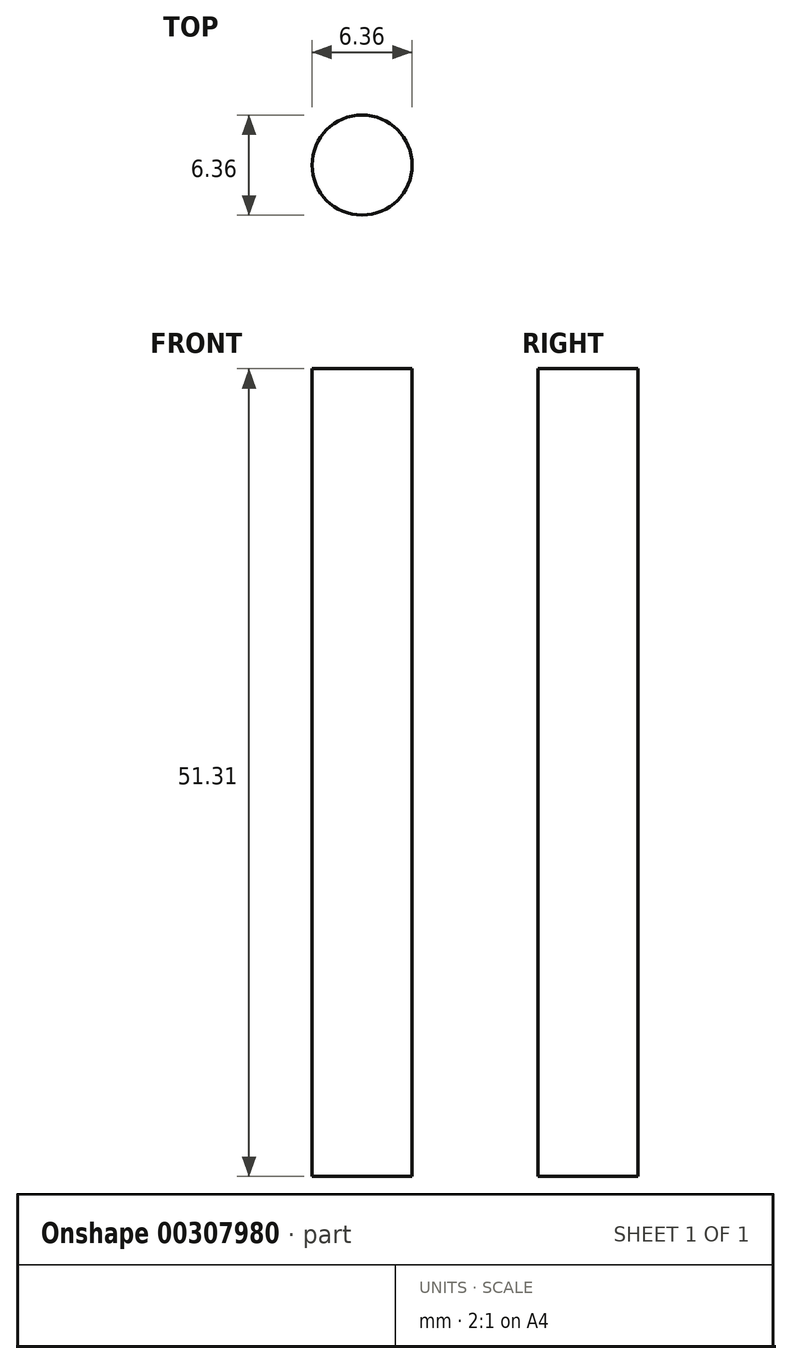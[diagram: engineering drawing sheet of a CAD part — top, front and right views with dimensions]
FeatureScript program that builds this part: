
annotation { "Feature Type Name" : "Feature", "Feature Type Description" : "" }
export const myFeature = defineFeature(function(context is Context, id is Id, definition is map)
    precondition{}
    {
        {
            var Q0;
            Q0=qCreatedBy(makeId("Top.planeOp"),FACE);
            var sketch = newSketch(context, id + "F0", { "sketchPlane" : qUnion([Q0])});
            skCircle(sketch, "E0", {"center": v(0, 0) * mm, "radius": 3.17 * mm});
            skSolve(sketch);
        }
        {
            var Q0;
            Q0 = qSketchRegion(id + "F0", true);
            extrude(context, id + "F1", {"entities" : qUnion([Q0]), "depth" : 51.3 * mm});
        }
    });
